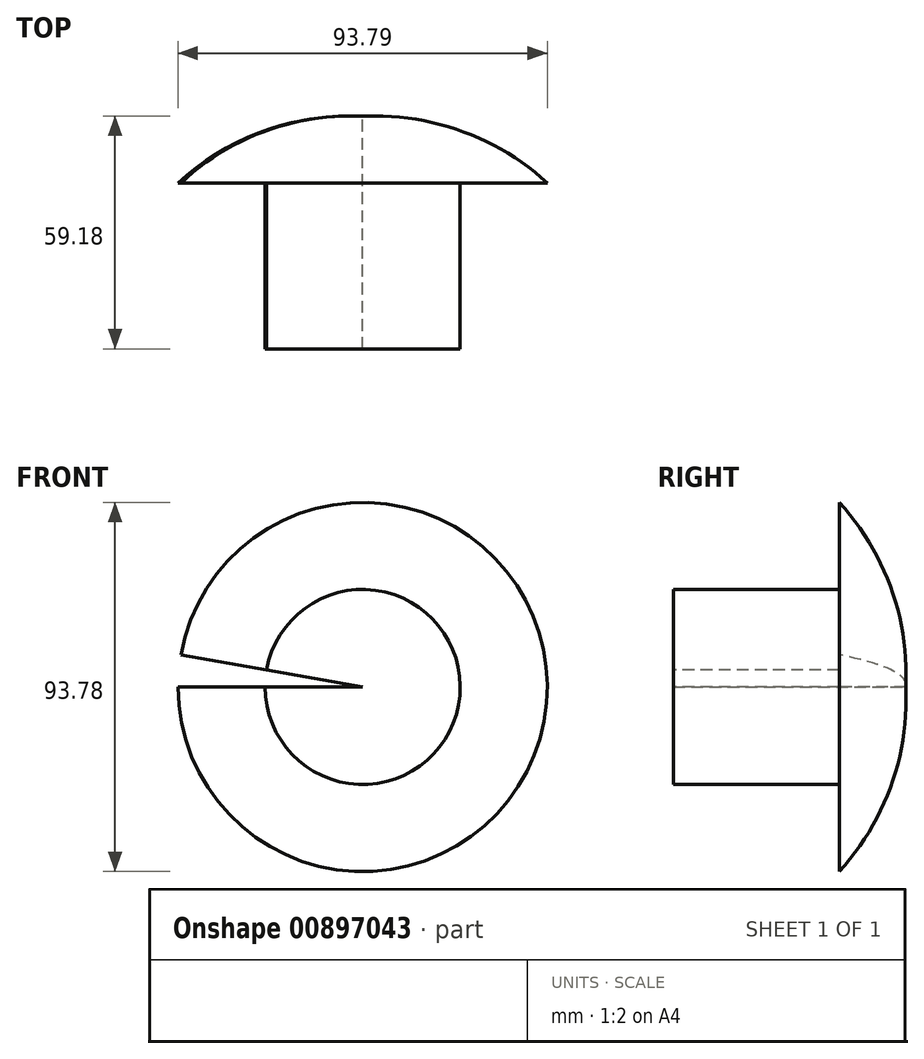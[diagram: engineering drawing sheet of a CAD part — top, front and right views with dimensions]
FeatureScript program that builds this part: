
annotation { "Feature Type Name" : "Feature", "Feature Type Description" : "" }
export const myFeature = defineFeature(function(context is Context, id is Id, definition is map)
    precondition{}
    {
        {
            var Q0;
            Q0=qCreatedBy(makeId("Top.planeOp"),FACE);
            var sketch = newSketch(context, id + "F0", { "sketchPlane" : qUnion([Q0])});
            skLineSegment(sketch, "E0", {"start": v(0, 0) * mm, "end": v(24.78, 0) * mm});
            skLineSegment(sketch, "E1", {"start": v(24.78, 0) * mm, "end": v(24.78, 59.1) * mm});
            skArc(sketch, "E2", {"start": v(24.78, 59.1) * mm, "mid": v(-0.36, 55.33) * mm, "end": v(-22.12, 42.18) * mm});
            skLineSegment(sketch, "E3", {"start": v(-22.12, 42.18) * mm, "end": v(0, 42.18) * mm});
            skLineSegment(sketch, "E4", {"start": v(0, 42.18) * mm, "end": v(0, 0) * mm});
            skSolve(sketch);
        }
        {
            var Q0;
            Q0=makeQuery(id+"F0.imprint","IMPRINT",FACE,{"disambiguationData":[TD([[makeQuery(id+"F0.imprint","IMPRINT",EDGE,{"derivedFrom":sQuery(id+"F0.wireOp",EDGE,"E0")}),1.0]])]});
            var Q1;
            Q1=sQuery(id+"F0.wireOp",EDGE,"E1");
            revolve(context, id + "F1", {"surfaceOperationType" : NewSurfaceOperationType.NEW, "entities" : qUnion([Q0]), "axis" : qUnion([Q1]), "revolveType" : RevolveType.ONE_DIRECTION, "oppositeDirection" : true, "angle" : 350 * degree});
        }
    });
